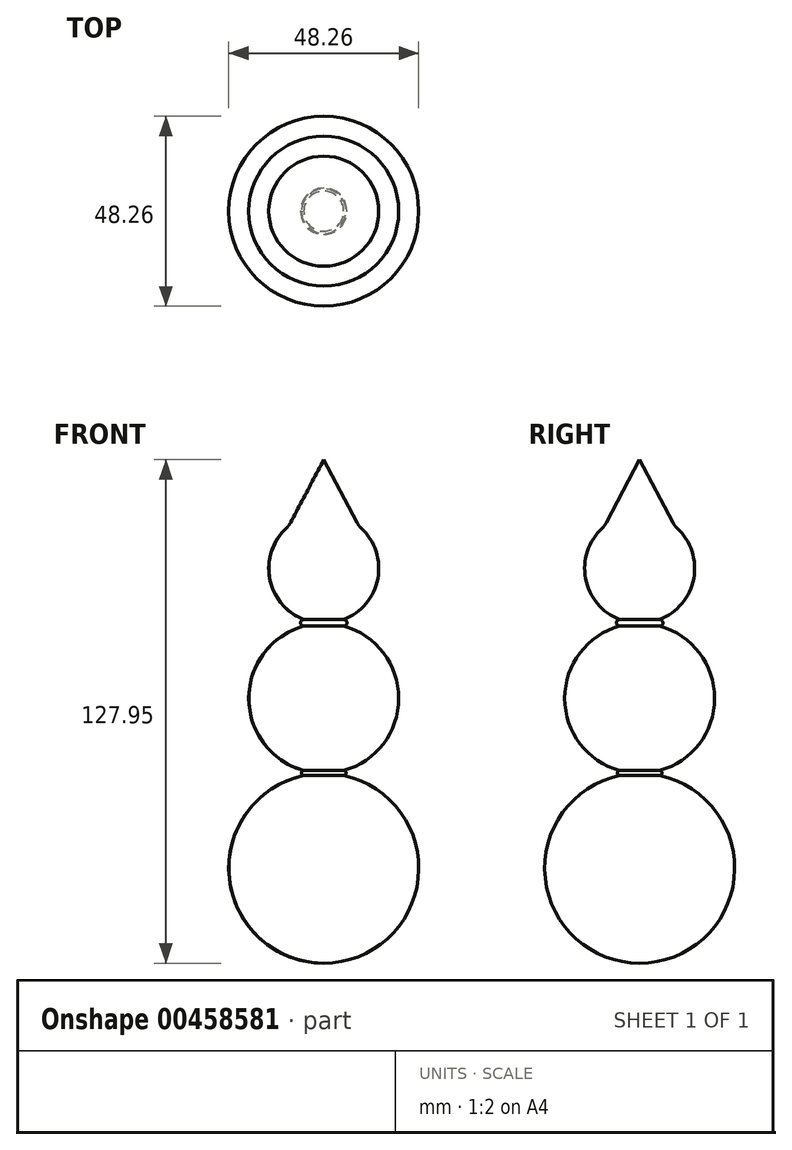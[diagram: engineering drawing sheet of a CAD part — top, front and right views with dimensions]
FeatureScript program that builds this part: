
annotation { "Feature Type Name" : "Feature", "Feature Type Description" : "" }
export const myFeature = defineFeature(function(context is Context, id is Id, definition is map)
    precondition{}
    {
        {
            var Q0;
            Q0=qCreatedBy(makeId("Front.planeOp"),FACE);
            var sketch = newSketch(context, id + "F0", { "sketchPlane" : qUnion([Q0])});
            skLineSegment(sketch, "E0", {"start": v(0, 0) * mm, "end": v(0, 38.1) * mm});
            skArc(sketch, "E1", {"start": v(0, 0) * mm, "mid": v(19.05, 19.05) * mm, "end": v(0, 38.1) * mm});
            skLineSegment(sketch, "E2", {"start": v(0, 38.1) * mm, "end": v(0, 66.04) * mm});
            skArc(sketch, "E3", {"start": v(0, 38.1) * mm, "mid": v(13.97, 52.07) * mm, "end": v(0, 66.04) * mm});
            skLineSegment(sketch, "E4", {"start": v(0, 0) * mm, "end": v(0, -48.26) * mm});
            skArc(sketch, "E5", {"start": v(0, -48.26) * mm, "mid": v(24.13, -24.13) * mm, "end": v(0, 0) * mm});
            skArc(sketch, "E6", {"start": v(13.7, 49.33) * mm, "mid": v(10.8, 60.93) * mm, "end": v(0, 66.04) * mm});
            skLineSegment(sketch, "E7", {"start": v(8.89, 62.85) * mm, "end": v(0, 79.7) * mm});
            skLineSegment(sketch, "E8", {"start": v(0, 79.7) * mm, "end": v(0, 66.04) * mm});
            skArc(sketch, "E9", {"start": v(5.08, -0.54) * mm, "mid": v(5.7, 0.07) * mm, "end": v(5.08, 0.69) * mm});
            skArc(sketch, "E10", {"start": v(5.08, 37.41) * mm, "mid": v(5.9, 38.23) * mm, "end": v(5.08, 39.06) * mm});
            skSolve(sketch);
        }
        {
            var Q0;
            Q0 = qSketchRegion(id + "F0", true);
            var Q1;
            Q1=sQuery(id+"F0.wireOp",EDGE,"E0");
            revolve(context, id + "F1", {"surfaceOperationType" : NewSurfaceOperationType.NEW, "entities" : qUnion([Q0]), "axis" : qUnion([Q1]), "revolveType" : RevolveType.FULL});
        }
        {
            var Q0;
            Q0=makeQuery(id+"F1.opRevolve","SWEPT_EDGE",EDGE,{"disambiguationData":[OSD([sQuery(id+"F0.wireOp",EDGE,"E6"),sQuery(id+"F0.wireOp",EDGE,"E7")])]});
            fillet(context, id + "F2", {"entities" : qUnion([Q0]), "radius" : 5.08 * mm, "tangentPropagation" : true, "allowEdgeOverflow" : false});
        }
    });
